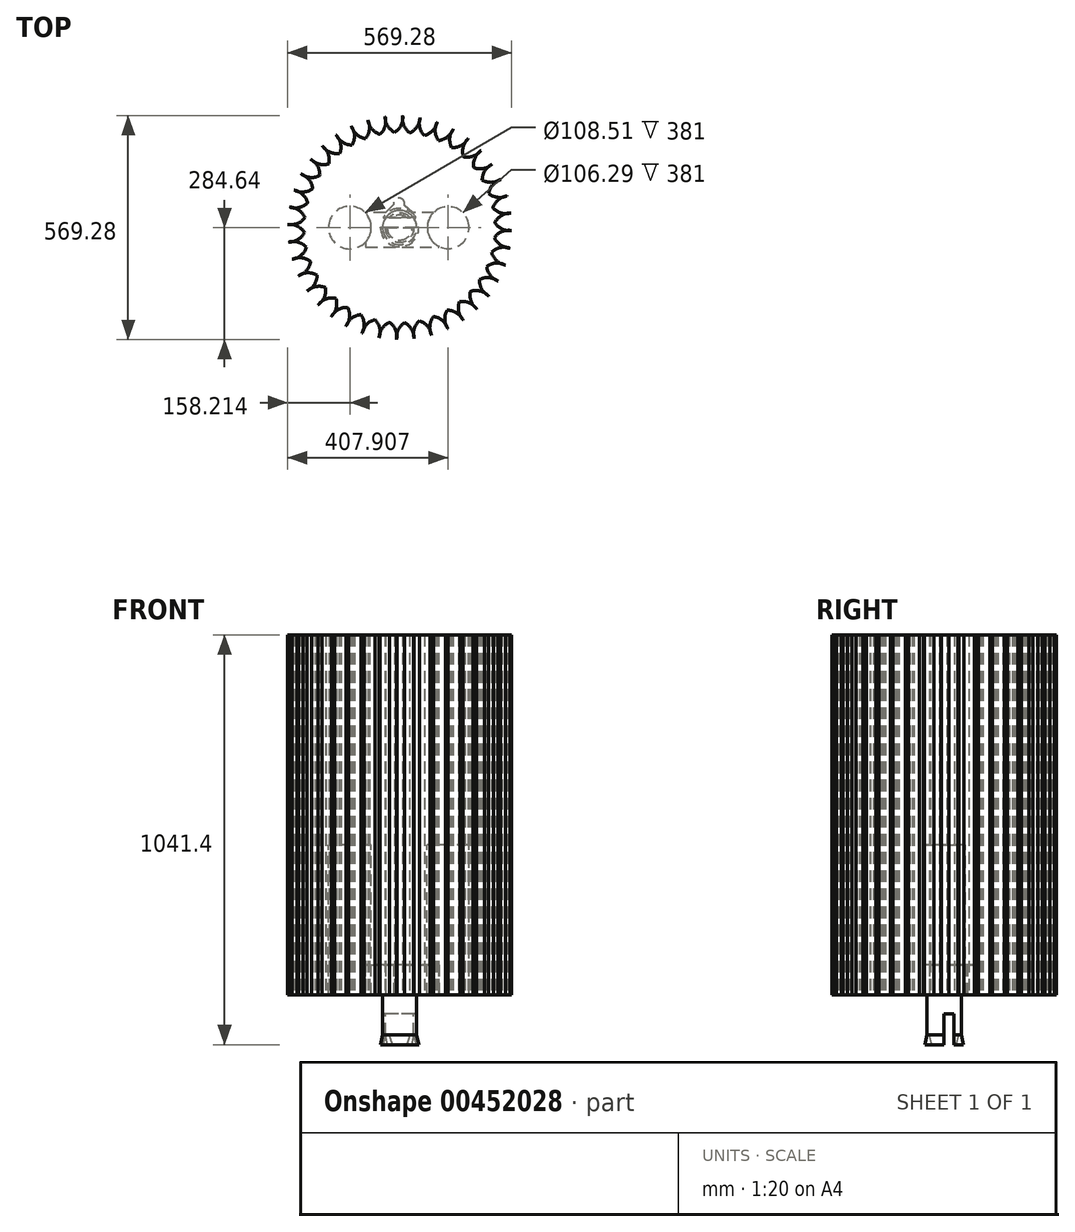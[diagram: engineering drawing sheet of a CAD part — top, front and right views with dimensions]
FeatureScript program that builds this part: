
annotation { "Feature Type Name" : "Feature", "Feature Type Description" : "" }
export const myFeature = defineFeature(function(context is Context, id is Id, definition is map)
    precondition{}
    {
        {
            var Q0;
            Q0=qCreatedBy(makeId("Top.planeOp"),FACE);
            var sketch = newSketch(context, id + "F0", { "sketchPlane" : qUnion([Q0])});
            skLineSegment(sketch, "E0", {"start": v(-16.06, 58.82) * mm, "end": v(-35.82, 38.42) * mm});
            skLineSegment(sketch, "E1", {"start": v(-35.82, 38.42) * mm, "end": v(-86.39, 38.42) * mm});
            skLineSegment(sketch, "E2", {"start": v(-86.39, 38.42) * mm, "end": v(-86.39, -49) * mm});
            skLineSegment(sketch, "E3", {"start": v(-86.39, -49) * mm, "end": v(99.4, -49) * mm});
            skLineSegment(sketch, "E4", {"start": v(99.4, -49) * mm, "end": v(101.66, 38.42) * mm});
            skLineSegment(sketch, "E5", {"start": v(101.66, 38.42) * mm, "end": v(32.92, 38.42) * mm});
            skLineSegment(sketch, "E6", {"start": v(32.92, 38.42) * mm, "end": v(12.31, 55.84) * mm});
            skArc(sketch, "E7", {"start": v(12.31, 55.84) * mm, "mid": v(-0.06, 74.64) * mm, "end": v(-16.06, 58.82) * mm});
            skSolve(sketch);
        }
        {
            var Q0;
            Q0 = qSketchRegion(id + "F0", true);
            extrude(context, id + "F1", {"entities" : qUnion([Q0]), "depth" : 76.2 * mm, "offsetDistance" : 25.4 * mm});
        }
        {
            var Q0;
            Q0=qCreatedBy(makeId("Top.planeOp"),FACE);
            var sketch = newSketch(context, id + "F2", { "sketchPlane" : qUnion([Q0])});
            skCircle(sketch, "E8", {"center": v(0, 0) * mm, "radius": 43.41 * mm});
            skSolve(sketch);
        }
        {
            var Q0;
            Q0 = qSketchRegion(id + "F2", true);
            extrude(context, id + "F3", {"entities" : qUnion([Q0]), "oppositeDirection" : true, "depth" : 101.6 * mm, "offsetDistance" : 25.4 * mm});
        }
        {
            var Q0;
            Q0=makeQuery(id+"F3.opExtrude","CAP_FACE",FACE,{"disambiguationData":[OSD([sQuery(id+"F2.wireOp",EDGE,"E8")])],"isStart":false});
            var sketch = newSketch(context, id + "F4", { "sketchPlane" : qUnion([Q0])});
            skCircle(sketch, "E9.0", {"center": v(0, 0) * mm, "radius": 43.41 * mm});
            skCircle(sketch, "E10", {"center": v(0, 0) * mm, "radius": 37.06 * mm});
            skSolve(sketch);
        }
        {
            var Q0;
            Q0 = qSketchRegion(id + "F4", true);
            extrude(context, id + "F5", {"entities" : qUnion([Q0]), "operationType" : NewBodyOperationType.ADD, "depth" : 25.4 * mm, "offsetDistance" : 25.4 * mm, "hasDraft" : true, "draftAngle" : 12 * degree});
        }
        {
            var Q0;
            Q0=qCreatedBy(makeId("Front.planeOp"),FACE);
            var sketch = newSketch(context, id + "F6", { "sketchPlane" : qUnion([Q0])});
            skLineSegment(sketch, "E11.bottom", {"start": v(58.75, -138.08) * mm, "end": v(-58.75, -138.08) * mm});
            skLineSegment(sketch, "E11.top", {"start": v(58.75, -48.79) * mm, "end": v(-58.75, -48.79) * mm});
            skLineSegment(sketch, "E11.left", {"start": v(58.75, -138.08) * mm, "end": v(58.75, -48.79) * mm});
            skLineSegment(sketch, "E11.right", {"start": v(-58.75, -138.08) * mm, "end": v(-58.75, -48.79) * mm});
            skPoint(sketch, "E11.middle", {"position": v(0, -93.44) * mm});
            skSolve(sketch);
        }
        {
            var Q0;
            Q0 = qSketchRegion(id + "F6", true);
            extrude(context, id + "F7", {"entities" : qUnion([Q0]), "operationType" : NewBodyOperationType.REMOVE, "oppositeDirection" : true, "depth" : 25.4 * mm, "offsetDistance" : 25.4 * mm});
        }
        {
            var Q0;
            Q0=qCreatedBy(makeId("Top.planeOp"),FACE);
            var sketch = newSketch(context, id + "F8", { "sketchPlane" : qUnion([Q0])});
            skCircle(sketch, "E12", {"center": v(0, 0) * mm, "radius": 317.5 * mm, "construction": true});
            skArc(sketch, "E13", {"start": v(19.51, -316.9) * mm, "mid": v(-6.42, -237.04) * mm, "end": v(-36.63, -315.38) * mm});
            skArc(sketch, "E14.1.0", {"start": v(68.85, -309.95) * mm, "mid": v(30.74, -235.13) * mm, "end": v(13.16, -317.23) * mm});
            skArc(sketch, "E14.2.0", {"start": v(116.48, -295.36) * mm, "mid": v(67.15, -227.42) * mm, "end": v(62.63, -311.26) * mm});
            skArc(sketch, "E14.3.0", {"start": v(161.25, -273.5) * mm, "mid": v(101.9, -214.12) * mm, "end": v(110.55, -297.63) * mm});
            skArc(sketch, "E14.4.0", {"start": v(202.05, -244.9) * mm, "mid": v(134.14, -195.54) * mm, "end": v(155.75, -276.68) * mm});
            skArc(sketch, "E14.5.0", {"start": v(237.88, -210.28) * mm, "mid": v(163.08, -172.15) * mm, "end": v(197.1, -248.9) * mm});
            skArc(sketch, "E14.6.0", {"start": v(267.85, -170.48) * mm, "mid": v(188, -144.52) * mm, "end": v(233.62, -215) * mm});
            skArc(sketch, "E14.7.0", {"start": v(291.22, -126.48) * mm, "mid": v(208.3, -113.33) * mm, "end": v(264.38, -175.81) * mm});
            skArc(sketch, "E14.8.0", {"start": v(307.42, -79.37) * mm, "mid": v(223.46, -79.35) * mm, "end": v(288.63, -132.3) * mm});
            skArc(sketch, "E14.9.0", {"start": v(316.05, -30.3) * mm, "mid": v(233.12, -43.42) * mm, "end": v(305.77, -85.51) * mm});
            skArc(sketch, "E14.10.0", {"start": v(316.9, 19.51) * mm, "mid": v(237.04, -6.42) * mm, "end": v(315.38, -36.63) * mm});
            skArc(sketch, "E14.11.0", {"start": v(309.95, 68.85) * mm, "mid": v(235.13, 30.74) * mm, "end": v(317.23, 13.16) * mm});
            skArc(sketch, "E14.12.0", {"start": v(295.36, 116.48) * mm, "mid": v(227.42, 67.15) * mm, "end": v(311.26, 62.63) * mm});
            skArc(sketch, "E14.13.0", {"start": v(273.5, 161.25) * mm, "mid": v(214.12, 101.9) * mm, "end": v(297.63, 110.55) * mm});
            skArc(sketch, "E14.14.0", {"start": v(244.9, 202.05) * mm, "mid": v(195.54, 134.14) * mm, "end": v(276.68, 155.75) * mm});
            skArc(sketch, "E14.15.0", {"start": v(210.28, 237.88) * mm, "mid": v(172.15, 163.08) * mm, "end": v(248.9, 197.1) * mm});
            skArc(sketch, "E14.16.0", {"start": v(170.48, 267.85) * mm, "mid": v(144.52, 188) * mm, "end": v(215, 233.62) * mm});
            skArc(sketch, "E14.17.0", {"start": v(126.48, 291.22) * mm, "mid": v(113.33, 208.3) * mm, "end": v(175.81, 264.38) * mm});
            skArc(sketch, "E14.18.0", {"start": v(79.37, 307.42) * mm, "mid": v(79.35, 223.46) * mm, "end": v(132.3, 288.63) * mm});
            skArc(sketch, "E14.19.0", {"start": v(30.3, 316.05) * mm, "mid": v(43.42, 233.12) * mm, "end": v(85.51, 305.77) * mm});
            skArc(sketch, "E14.20.0", {"start": v(-19.51, 316.9) * mm, "mid": v(6.42, 237.04) * mm, "end": v(36.63, 315.38) * mm});
            skArc(sketch, "E14.21.0", {"start": v(-68.85, 309.95) * mm, "mid": v(-30.74, 235.13) * mm, "end": v(-13.16, 317.23) * mm});
            skArc(sketch, "E14.22.0", {"start": v(-116.48, 295.36) * mm, "mid": v(-67.15, 227.42) * mm, "end": v(-62.63, 311.26) * mm});
            skArc(sketch, "E14.23.0", {"start": v(-161.25, 273.5) * mm, "mid": v(-101.9, 214.12) * mm, "end": v(-110.55, 297.63) * mm});
            skArc(sketch, "E14.24.0", {"start": v(-202.05, 244.9) * mm, "mid": v(-134.14, 195.54) * mm, "end": v(-155.75, 276.68) * mm});
            skArc(sketch, "E14.25.0", {"start": v(-237.88, 210.28) * mm, "mid": v(-163.08, 172.15) * mm, "end": v(-197.1, 248.9) * mm});
            skArc(sketch, "E14.26.0", {"start": v(-267.85, 170.48) * mm, "mid": v(-188, 144.52) * mm, "end": v(-233.62, 215) * mm});
            skArc(sketch, "E14.27.0", {"start": v(-291.22, 126.48) * mm, "mid": v(-208.3, 113.33) * mm, "end": v(-264.38, 175.81) * mm});
            skArc(sketch, "E14.28.0", {"start": v(-307.42, 79.37) * mm, "mid": v(-223.46, 79.35) * mm, "end": v(-288.63, 132.3) * mm});
            skArc(sketch, "E14.29.0", {"start": v(-316.05, 30.3) * mm, "mid": v(-233.12, 43.42) * mm, "end": v(-305.77, 85.51) * mm});
            skArc(sketch, "E14.30.0", {"start": v(-316.9, -19.51) * mm, "mid": v(-237.04, 6.42) * mm, "end": v(-315.38, 36.63) * mm});
            skArc(sketch, "E14.31.0", {"start": v(-309.95, -68.85) * mm, "mid": v(-235.13, -30.74) * mm, "end": v(-317.23, -13.16) * mm});
            skArc(sketch, "E14.32.0", {"start": v(-295.36, -116.48) * mm, "mid": v(-227.42, -67.15) * mm, "end": v(-311.26, -62.63) * mm});
            skArc(sketch, "E14.33.0", {"start": v(-273.5, -161.25) * mm, "mid": v(-214.12, -101.9) * mm, "end": v(-297.63, -110.55) * mm});
            skArc(sketch, "E14.34.0", {"start": v(-244.9, -202.05) * mm, "mid": v(-195.54, -134.14) * mm, "end": v(-276.68, -155.75) * mm});
            skArc(sketch, "E14.35.0", {"start": v(-210.28, -237.88) * mm, "mid": v(-172.15, -163.08) * mm, "end": v(-248.9, -197.1) * mm});
            skArc(sketch, "E14.36.0", {"start": v(-170.48, -267.85) * mm, "mid": v(-144.52, -188) * mm, "end": v(-215, -233.62) * mm});
            skArc(sketch, "E14.37.0", {"start": v(-126.48, -291.22) * mm, "mid": v(-113.33, -208.3) * mm, "end": v(-175.81, -264.38) * mm});
            skArc(sketch, "E14.38.0", {"start": v(-79.37, -307.42) * mm, "mid": v(-79.35, -223.46) * mm, "end": v(-132.3, -288.63) * mm});
            skArc(sketch, "E14.39.0", {"start": v(-30.3, -316.05) * mm, "mid": v(-43.42, -233.12) * mm, "end": v(-85.51, -305.77) * mm});
            skSolve(sketch);
        }
        {
            var Q0;
            Q0 = qSketchRegion(id + "F8", true);
            extrude(context, id + "F9", {"entities" : qUnion([Q0]), "depth" : 914.4 * mm, "offsetDistance" : 25.4 * mm});
        }
        {
            var Q0;
            Q0=qCreatedBy(makeId("Top.planeOp"),FACE);
            cPlane(context, id + "F10", {"entities" : qUnion([Q0]), "cplaneType" : CPlaneType.OFFSET, "offset" : 381 * mm, "width" : 152.4 * mm, "height" : 152.4 * mm});
        }
        {
            var Q0;
            Q0=qCreatedBy(id+"F10.planeOp",FACE);
            var sketch = newSketch(context, id + "F11", { "sketchPlane" : qUnion([Q0])});
            skPoint(sketch, "E15.0", {"position": v(0, 0) * mm});
            skCircle(sketch, "E16", {"center": v(123.27, 0) * mm, "radius": 53.14 * mm});
            skCircle(sketch, "E17", {"center": v(-126.43, 0) * mm, "radius": 54.25 * mm});
            skSolve(sketch);
        }
        {
            var Q0;
            Q0 = qSketchRegion(id + "F11", true);
            extrude(context, id + "F12", {"entities" : qUnion([Q0]), "operationType" : NewBodyOperationType.REMOVE, "oppositeDirection" : true, "depth" : 508 * mm, "offsetDistance" : 25.4 * mm});
        }
    });
